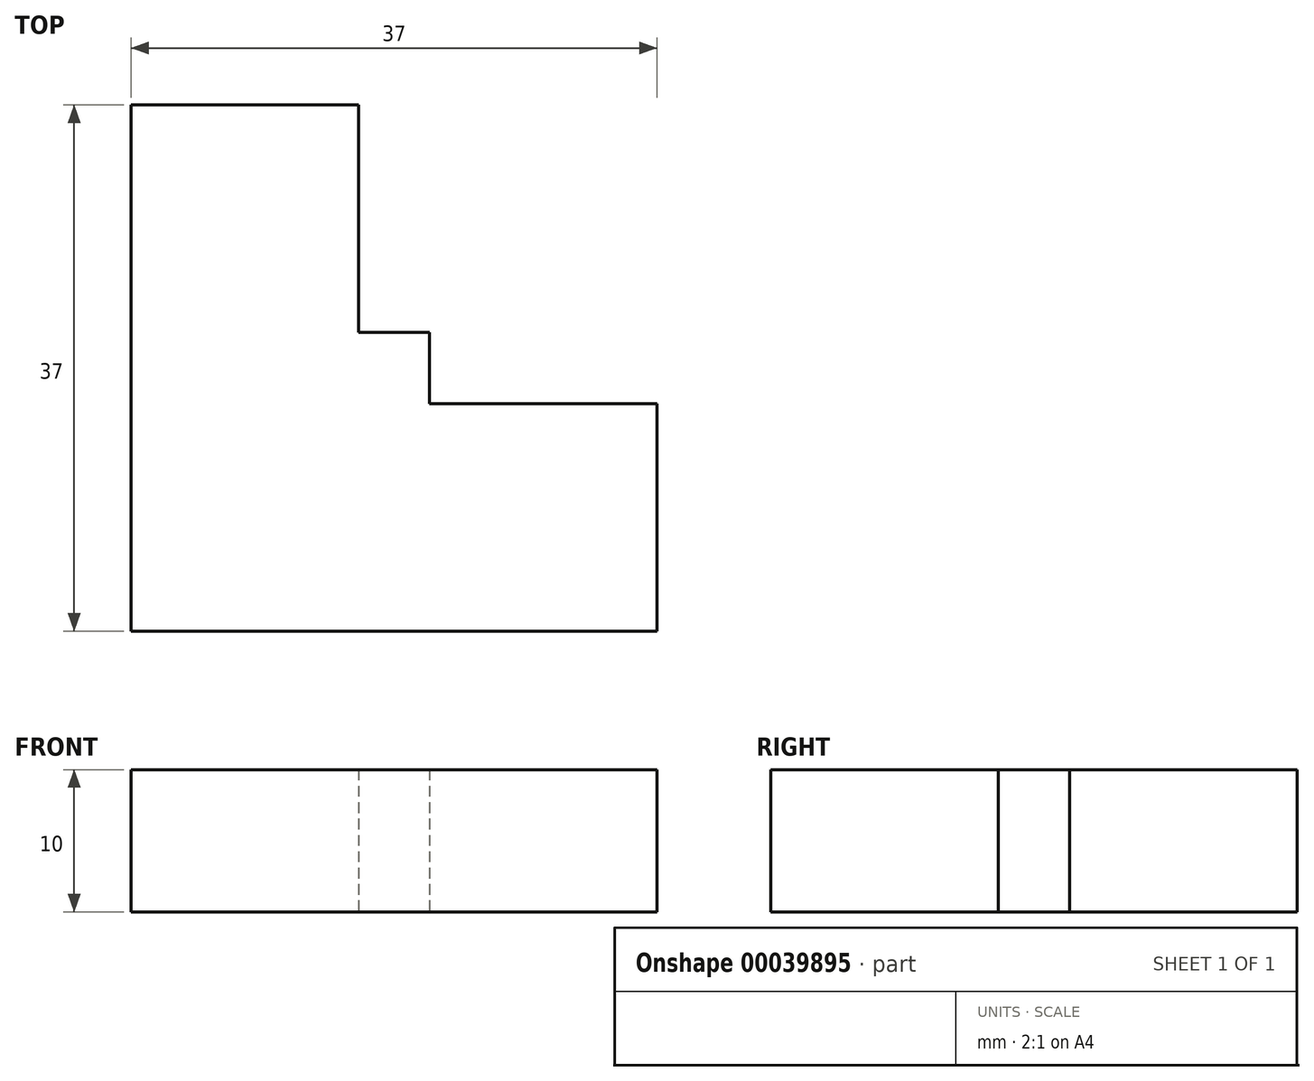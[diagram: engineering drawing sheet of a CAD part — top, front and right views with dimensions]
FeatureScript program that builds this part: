
annotation { "Feature Type Name" : "Feature", "Feature Type Description" : "" }
export const myFeature = defineFeature(function(context is Context, id is Id, definition is map)
    precondition{}
    {
        {
            var Q0;
            Q0=qCreatedBy(makeId("Top.planeOp"),FACE);
            var sketch = newSketch(context, id + "F0", { "sketchPlane" : qUnion([Q0])});
            skLineSegment(sketch, "E0.bottom", {"start": v(-29.04, 22.35) * mm, "end": v(-8.04, 22.35) * mm});
            skLineSegment(sketch, "E0.top", {"start": v(-29.04, 1.35) * mm, "end": v(-8.04, 1.35) * mm});
            skLineSegment(sketch, "E0.left", {"start": v(-29.04, 22.35) * mm, "end": v(-29.04, 1.35) * mm});
            skLineSegment(sketch, "E0.right", {"start": v(-8.04, 22.35) * mm, "end": v(-8.04, 1.35) * mm});
            skLineSegment(sketch, "E1.left", {"start": v(-8.04, 17.35) * mm, "end": v(-8.04, 1.35) * mm});
            skLineSegment(sketch, "E2.bottom", {"start": v(-29.04, 22.35) * mm, "end": v(-13.04, 22.35) * mm});
            skLineSegment(sketch, "E2.top", {"start": v(-29.04, 38.35) * mm, "end": v(-13.04, 38.35) * mm});
            skLineSegment(sketch, "E2.left", {"start": v(-29.04, 22.35) * mm, "end": v(-29.04, 38.35) * mm});
            skLineSegment(sketch, "E2.right", {"start": v(-13.04, 22.35) * mm, "end": v(-13.04, 38.35) * mm});
            skLineSegment(sketch, "E3", {"start": v(-8.04, 1.35) * mm, "end": v(7.96, 1.35) * mm});
            skLineSegment(sketch, "E4", {"start": v(-8.04, 17.35) * mm, "end": v(7.96, 17.35) * mm});
            skLineSegment(sketch, "E5", {"start": v(7.96, 17.35) * mm, "end": v(7.96, 1.35) * mm});
            skSolve(sketch);
        }
        {
            var Q0;
            Q0 = qSketchRegion(id + "F0", true);
            extrude(context, id + "F1", {"entities" : qUnion([Q0]), "depth" : 10 * mm});
        }
    });
